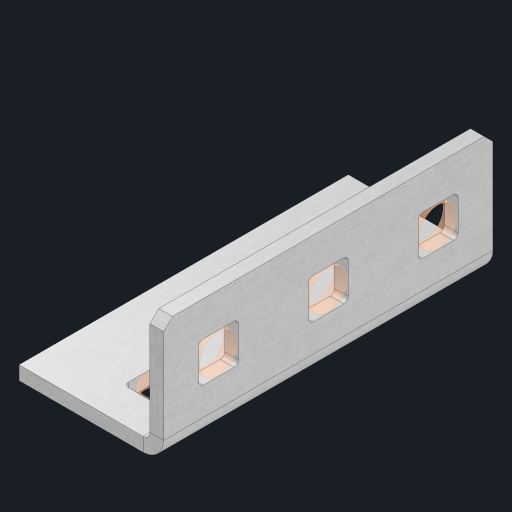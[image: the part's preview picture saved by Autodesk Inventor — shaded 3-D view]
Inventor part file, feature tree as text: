
AUTODESK INVENTOR PART (.ipt)
format: ipt  version: 2023 (Build 270158000, 158)  size: 471,552 bytes
history: native  units: in
note: dims shown in document units (in); Inventor stores cm internally (conversion verified against a paired STEP export)
features: other x11, sheet_metal_op x10, sketch x8, extrude x5, mirror x1, pattern_linear x1, chamfer x1
ambient origin geometry x8: Origin, YZ Plane, XZ Plane, XY Plane, X Axis, Y Axis, Z Axis, Center Point
bodies: Solid1 (feature_tree), Body (feature_tree)
feature tree (37):
  other  "Flange Pattern Plane"
  sheet_metal_op  "Flange Pattern"
  sheet_metal_op  "Body Pattern"
  other  "Arc Length"
  mirror  "Notch Mirror"
  pattern_linear  "Notch Pattern"  Spacing1=0.25in  [1 undecoded]
  chamfer  "End Chamfer"
  extrude  "Half Cut"  Depth=0.0625in
  sketch  "Sketch1"  dims[d0=1.5in]
  other  "Plate1"
  sketch  "Sketch2"  dims[d1=1.5in]
  other  "Plate2"
  sheet_metal_op  "Bend1"
  sheet_metal_op  "Corner1"
  sketch  "Sketch3"  dims[d2=0.0625in]
  other  "Flange Pattern Sketch"
  sketch  "Sketch7"  dims[d3=0.0625in]
  other  "Srf1"
  other  "Srf2"
  sketch  "Sketch8"  dims[d4=0.0312in]
  sketch  "Sketch9"  dims[d5=0.125in]
  other  "Srf91"
  sheet_metal_op  "Body Pattern Sketch"
  other  "Srf92"
  sketch  "Sketch13"  dims[d6=0.0625in]
  sketch  "Sketch14"  dims[d7=0.5in d8=90.0deg d9=0.0312in d10=0.25in d11=0.0625in d12=0.0625in d16=0.182in d17=0.02in d18=0.0625in d19=0.0in d20=0.25in d21=0.25in d46=0.172in d47=1.0in d48=0.0in d49=0.182in d50=0.02in d51=0.25in d52=0.25in d53=0.0625in d54=0.0in d55=0.172in d56=1.0in d57=0.0in d60=1.1811in d62=0.5in d63=0.3937in d65=0.5in d85=0.1473in d86=0.1782in d88=0.04in d89=0.0625in d90=0.0in d91=0.04in d92=0.0491in d95=2.5in d96=0.04in d97=0.25in d98=45.0deg d101=0.0in d102=2.497in d131=0.5in d132=1.1811in d134=0.5in d139=0.5in]
  other  "Srf856"
  other  "Srf1310"
  sheet_metal_op  "Flange Stamp"
  sheet_metal_op  "Flange Circle"
  sheet_metal_op  "Body Stamp"
  sheet_metal_op  "Body Circle"
  sheet_metal_op  "Notch"
  extrude  "ExtrusionSrf2"  Depth=0.0625in
  extrude  "ExtrusionSrf92"  Depth=0.182in
  extrude  "ExtrusionSrf856"  Depth=0.02in
  extrude  "ExtrusionSrf1310"  Depth=0.0625in
note: 1 required parameter value undecoded (feature->parameter linkage not recoverable at this tier; creation-order binding heuristic only, values carry confidence <= 0.55)
